# Revit family: Resideo_HR_RadiatorController_HR90a
name_source: partatom
category: Electrical Fixtures
units: mm (PartAtom-declared; Revit-internal decimal feet)

## family parameters
Cut with Voids When Loaded = No
Host = Face
Maintain Annotation Orientation = No
OmniClass Number = 23.75.65.11.11
OmniClass Title = Heating Controllers
Part Type = Normal
Room Calculation Point = No
Round Connector Dimension = Use Diameter
Shared = No

## types (1)
- HR90
    Assembly Code = D3060
    AssetType = Fixed
    BIMObjectName = Resideo_HR_RadiatorController_HR90
    ClassificationName = Uniclass2015
    ClassificationValue = Pr_75_50_76_73
    Cost = 0 $
    Default Elevation = 0 mm  [stored 0 ft]
    Description = HR90 Locally Programmable Electronic Thermostatic Radiator Valve Controller
    DisplayMaterial = Resideo - Screen - Grey
    DocumentationCertificates = https://www.bimstore.co
    DocumentationInstallationGuide = https://www.bimstore.co
    DocumentationLiterature = https://www.bimstore.co
    DocumentationMaintenance = https://www.bimstore.co
    DocumentationTechnical = https://www.bimstore.co
    DurationUnit = Years
    ExpectedLife = 0
    IfcExportAs = IfcUnitaryControlElement
    IfcExportType = IfcUnitaryControlElementTypeEnum.CONTROLPANEL
    Keynote = W
    Manufacturer = Resideo
    ManufacturerName = Resideo
    Model = HR90
    ModelNumber = HR90
    ModelReference = HR90 Locally Programmable Electronic Thermostatic Radiator Valve Controller
    NBSDescription = Room temperature sensors
    NBSObjectName = Resideo - Room temperature sensors
    NominalDepth = 55 mm
    NominalHeight = 55 mm
    NominalLength = 97 mm
    PrimaryMaterial = Resideo - Plastic - White
    ProductionYear = 2022
    Size = 55mm (D) x 55mm (H) x 97mm (L)
    Type Comments = HR90 Locally Programmable Electronic Thermostatic Radiator Valve Controller
    TypeName = HR90 - HR90 Locally Programmable Electronic Thermostatic Radiator Valve Controller
    URL = https://www.resideo.com
    WarrantyDurationLabor = 0
    WarrantyDurationParts = 0
    WarrantyDurationUnit = Years
    WarrantyGuarantorLabor = https://www.resideo.com
    WarrantyGuarantorParts = https://www.resideo.com
    _BSBibleVersion = 16
    _BimSpecGuid = 0
    _CurrentRevision = 1
    _DistributedBy = https://www.bimstore.co
    _ObjectUserGuide = https://www.bimstore.co

note: [stored X ft] marks values corroborated as IEEE doubles in the binary element streams (Revit-internal decimal feet)

## geometry (parser evidence)
native form markers: Sweep x2
no freeform markers — native parametric forms only
